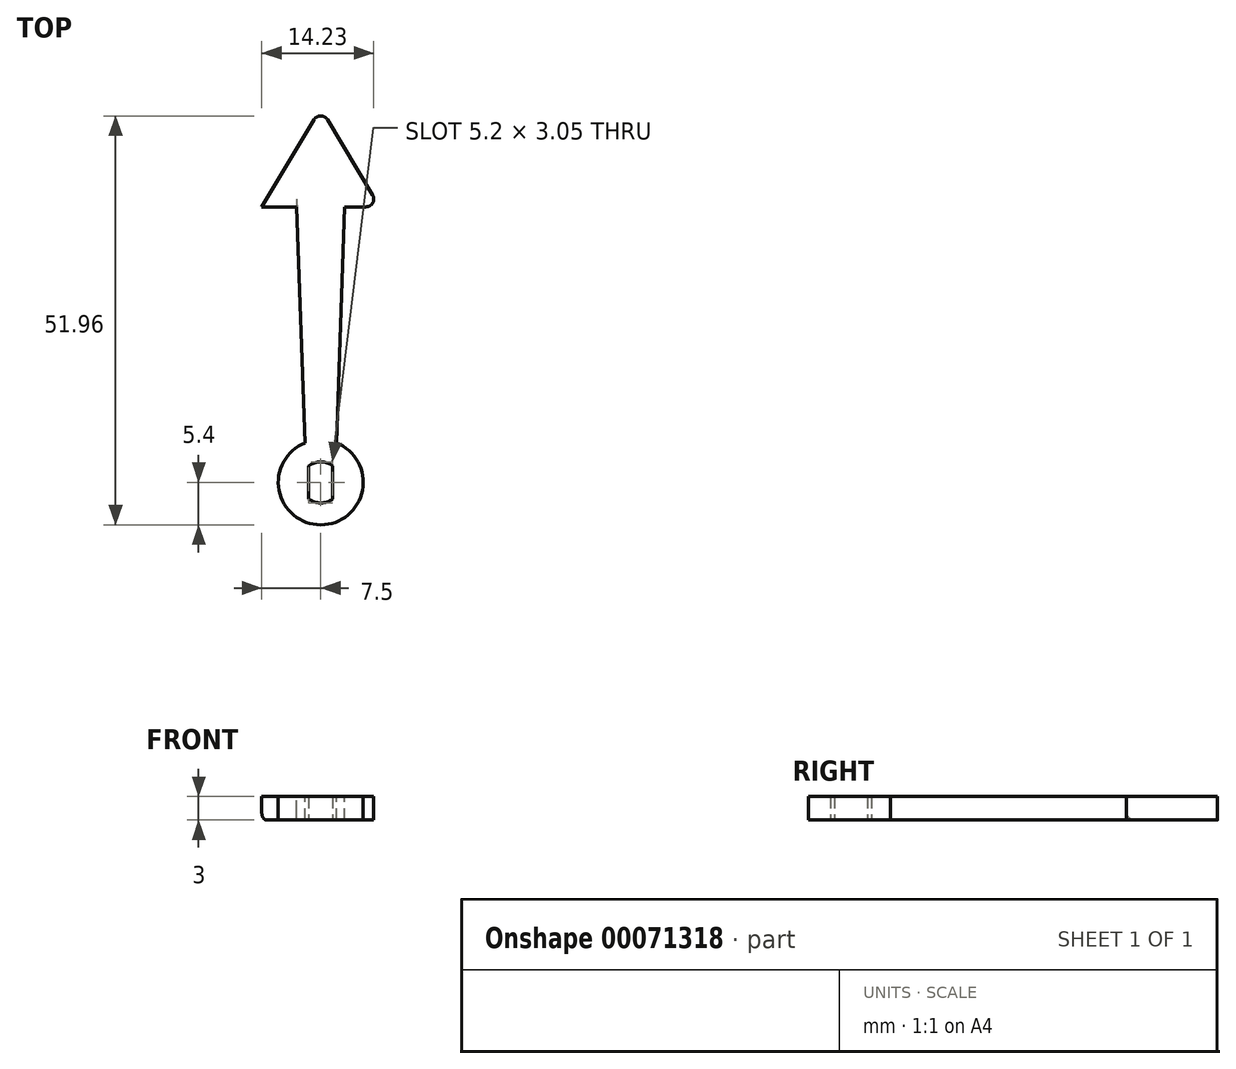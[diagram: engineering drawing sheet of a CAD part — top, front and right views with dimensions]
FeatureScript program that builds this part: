
annotation { "Feature Type Name" : "Feature", "Feature Type Description" : "" }
export const myFeature = defineFeature(function(context is Context, id is Id, definition is map)
    precondition{}
    {
        {
            var Q0;
            Q0=qCreatedBy(makeId("Top.planeOp"),FACE);
            var sketch = newSketch(context, id + "F0", { "sketchPlane" : qUnion([Q0])});
            skCircle(sketch, "E0", {"center": v(0, 0) * mm, "radius": 5.4 * mm});
            skCircle(sketch, "E1", {"center": v(0, 0) * mm, "radius": 2.6 * mm});
            skLineSegment(sketch, "E2", {"start": v(-1.52, 2.1) * mm, "end": v(-1.52, -2.1) * mm});
            skLineSegment(sketch, "E3", {"start": v(1.53, 2.1) * mm, "end": v(1.53, -2.1) * mm});
            skSolve(sketch);
        }
        {
            var Q0;
            Q0 = qSketchRegion(id + "F0", true);
            var Q1;
            {var subQ0=sQuery(id+"F0.wireOp",EDGE,"E2");Q1=makeQuery(id+"F0.imprint","IMPRINT",FACE,{"disambiguationData":[TD([[makeQuery(id+"F0.imprint","IMPRINT",EDGE,{"derivedFrom":subQ0}),-1.0]])]});}
            var Q2;
            {var subQ0=sQuery(id+"F0.wireOp",EDGE,"E3");Q2=makeQuery(id+"F0.imprint","IMPRINT",FACE,{"disambiguationData":[TD([[makeQuery(id+"F0.imprint","IMPRINT",EDGE,{"derivedFrom":subQ0}),1.0]])]});}
            extrude(context, id + "F1", {"entities" : qUnion([Q0, Q1, Q2]), "endBound" : BoundingType.SYMMETRIC, "depth" : 3 * mm});
        }
        {
            var Q0;
            Q0=makeQuery(id+"F1.opExtrude","CAP_FACE",FACE,{"disambiguationData":[OSD([sQuery(id+"F0.wireOp",EDGE,"E0"),sQuery(id+"F0.wireOp",EDGE,"E1"),sQuery(id+"F0.wireOp",EDGE,"E2"),sQuery(id+"F0.wireOp",EDGE,"E3")])],"isStart":false});
            var sketch = newSketch(context, id + "F2", { "sketchPlane" : qUnion([Q0])});
            skLineSegment(sketch, "E4", {"start": v(0, 0) * mm, "end": v(0, 35) * mm, "construction": true});
            skLineSegment(sketch, "E5", {"start": v(0, 35) * mm, "end": v(3.05, 35) * mm});
            skLineSegment(sketch, "E6", {"start": v(3.05, 35) * mm, "end": v(2, 5.02) * mm});
            skLineSegment(sketch, "E7", {"start": v(2, 5.02) * mm, "end": v(0, 5.02) * mm});
            skLineSegment(sketch, "E8.MirrorCS", {"start": v(-3.05, 35) * mm, "end": v(-2, 5.02) * mm});
            skLineSegment(sketch, "E9.MirrorCS", {"start": v(0, 35) * mm, "end": v(-3.05, 35) * mm});
            skLineSegment(sketch, "E10.MirrorCS", {"start": v(-2, 5.02) * mm, "end": v(0, 5.02) * mm});
            skSolve(sketch);
        }
        {
            var Q0;
            Q0=makeQuery(id+"F2.imprint","IMPRINT",FACE,{"disambiguationData":[TD([[makeQuery(id+"F2.imprint","IMPRINT",EDGE,{"derivedFrom":sQuery(id+"F2.wireOp",EDGE,"E5")}),-1.0]])]});
            var Q1;
            Q1=qCreatedBy(makeId("Top.planeOp"),FACE);
            var Q2;
            Q2=makeQuery(id+"F1.opExtrude","SWEPT_BODY",BODY,{"disambiguationData":[OSD([sQuery(id+"F0.wireOp",EDGE,"E0"),sQuery(id+"F0.wireOp",EDGE,"E1"),sQuery(id+"F0.wireOp",EDGE,"E2"),sQuery(id+"F0.wireOp",EDGE,"E3")])]});
            extrude(context, id + "F3", {"entities" : qUnion([Q0]), "operationType" : NewBodyOperationType.ADD, "endBound" : BoundingType.UP_TO_SURFACE, "oppositeDirection" : true, "endBoundEntityFace" : qUnion([Q1]), "endBoundEntityBody" : qUnion([Q2]), "depth" : 6.72 * mm});
        }
        {
            var Q0;
            Q0=makeQuery(id+"F1.opExtrude","SWEPT_BODY",BODY,{"disambiguationData":[OSD([sQuery(id+"F0.wireOp",EDGE,"E0"),sQuery(id+"F0.wireOp",EDGE,"E1"),sQuery(id+"F0.wireOp",EDGE,"E2"),sQuery(id+"F0.wireOp",EDGE,"E3")])]});
            var Q1;
            Q1=makeQuery(id+"F3.opExtrude","CAP_FACE",FACE,{"disambiguationData":[OSD([sQuery(id+"F0.wireOp",EDGE,"E0"),sQuery(id+"F2.wireOp",EDGE,"E5"),sQuery(id+"F2.wireOp",EDGE,"E6"),sQuery(id+"F2.wireOp",EDGE,"E8.MirrorCS"),sQuery(id+"F2.wireOp",EDGE,"E9.MirrorCS")])],"isStart":false});
            mirror(context, id + "F4", {"operationType" : NewBodyOperationType.ADD, "entities" : qUnion([Q0]), "mirrorPlane" : qUnion([Q1])});
        }
        {
            var Q0;
            Q0=qCreatedBy(makeId("Top.planeOp"),FACE);
            var sketch = newSketch(context, id + "F5", { "sketchPlane" : qUnion([Q0])});
            skLineSegment(sketch, "E11", {"start": v(0, 35) * mm, "end": v(0, 47.5) * mm, "construction": true});
            skLineSegment(sketch, "E12", {"start": v(-7.5, 35) * mm, "end": v(7.5, 35) * mm});
            skLineSegment(sketch, "E13", {"start": v(0, 47.5) * mm, "end": v(-7.5, 35) * mm});
            skLineSegment(sketch, "E14", {"start": v(0, 47.5) * mm, "end": v(7.5, 35) * mm});
            skSolve(sketch);
        }
        {
            var Q0;
            Q0=makeQuery(id+"F5.imprint","IMPRINT",FACE,{"disambiguationData":[TD([[makeQuery(id+"F5.imprint","IMPRINT",EDGE,{"derivedFrom":sQuery(id+"F5.wireOp",EDGE,"E12")}),1.0]])]});
            extrude(context, id + "F6", {"entities" : qUnion([Q0]), "operationType" : NewBodyOperationType.ADD, "endBound" : BoundingType.SYMMETRIC, "depth" : 3 * mm});
        }
        {
            var Q0;
            Q0=makeQuery(id+"F6.opExtrude","SWEPT_EDGE",EDGE,{"disambiguationData":[OSD([sQuery(id+"F5.wireOp",EDGE,"E13"),sQuery(id+"F5.wireOp",EDGE,"E14")])]});
            var Q1;
            Q1=makeQuery(id+"F6.opExtrude","SWEPT_EDGE",EDGE,{"disambiguationData":[OSD([sQuery(id+"F5.wireOp",EDGE,"E12"),sQuery(id+"F5.wireOp",EDGE,"E14")])]});
            var Q2;
            {var subQ0=sQuery(id+"F2.wireOp",EDGE,"E8.MirrorCS");var subQ5=makeQuery(id+"F3.opExtrude","SWEPT_FACE",FACE,{"disambiguationData":[OSD([subQ0])]});var subQ7=sQuery(id+"F5.wireOp",EDGE,"E12");Q2=makeQuery(id+"F6.boolean.opBoolean","SPLIT",EDGE,{"disambiguationData":[TD([subQ5])],"derivedFrom":makeQuery(id+"F6.opExtrude","CAP_EDGE",EDGE,{"disambiguationData":[OSD([subQ7])],"isStart":true})});}
            fillet(context, id + "F7", {"entities" : qUnion([Q0, Q1, Q2]), "radius" : 1 * mm, "tangentPropagation" : true, "allowEdgeOverflow" : false});
        }
    });
